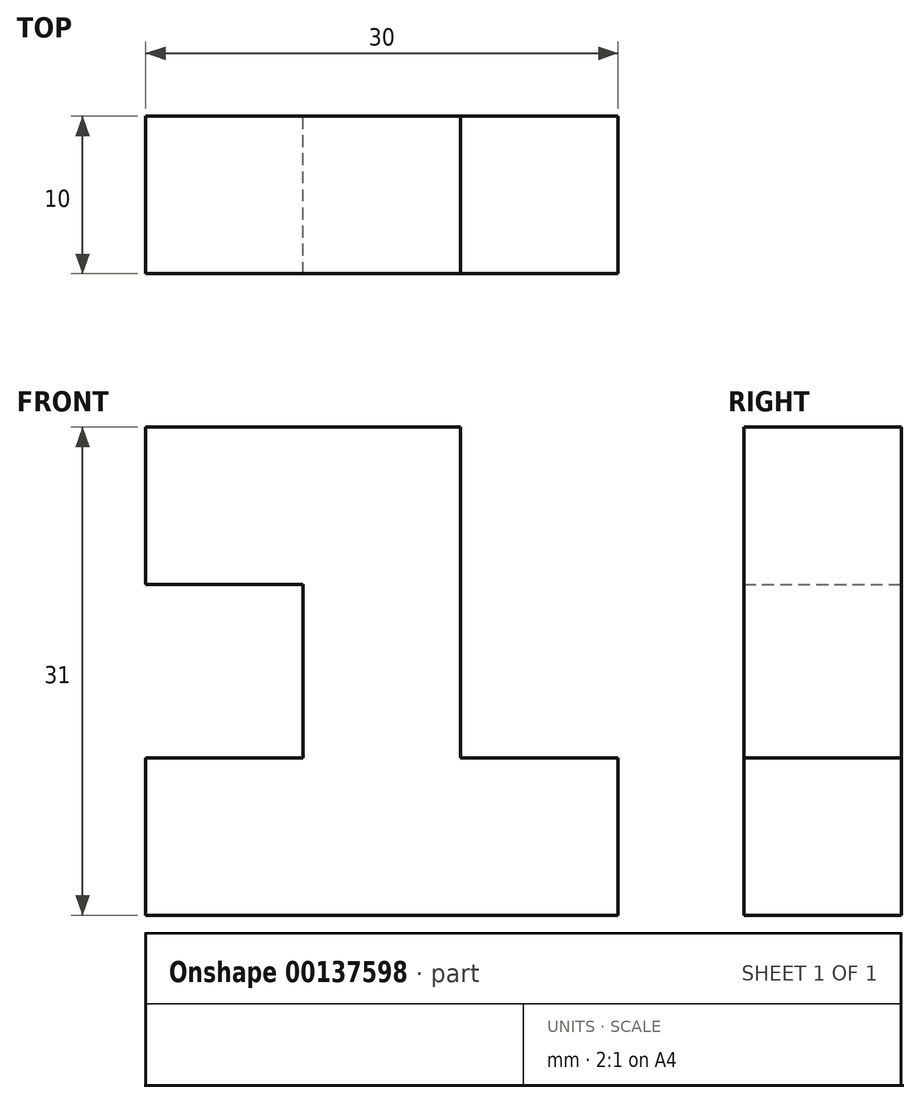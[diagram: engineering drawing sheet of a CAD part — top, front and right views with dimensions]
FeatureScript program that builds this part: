
annotation { "Feature Type Name" : "Feature", "Feature Type Description" : "" }
export const myFeature = defineFeature(function(context is Context, id is Id, definition is map)
    precondition{}
    {
        {
            var Q0;
            Q0=qCreatedBy(makeId("Front.planeOp"),FACE);
            var sketch = newSketch(context, id + "F0", { "sketchPlane" : qUnion([Q0])});
            skLineSegment(sketch, "E0", {"start": v(-31, 40.15) * mm, "end": v(-31, 30.15) * mm});
            skLineSegment(sketch, "E1", {"start": v(-21, 30.15) * mm, "end": v(-31, 30.15) * mm});
            skLineSegment(sketch, "E2", {"start": v(-21, 30.15) * mm, "end": v(-21, 19.15) * mm});
            skLineSegment(sketch, "E3", {"start": v(-21, 19.15) * mm, "end": v(-31, 19.15) * mm});
            skLineSegment(sketch, "E4", {"start": v(-31, 19.15) * mm, "end": v(-31, 9.15) * mm});
            skLineSegment(sketch, "E5", {"start": v(-31, 9.15) * mm, "end": v(-1, 9.15) * mm});
            skLineSegment(sketch, "E6", {"start": v(-1, 9.15) * mm, "end": v(-1, 19.15) * mm});
            skLineSegment(sketch, "E7", {"start": v(-1, 19.15) * mm, "end": v(-11, 19.15) * mm});
            skLineSegment(sketch, "E8", {"start": v(-11, 19.15) * mm, "end": v(-11, 40.15) * mm});
            skLineSegment(sketch, "E9", {"start": v(-11, 40.15) * mm, "end": v(-31, 40.15) * mm});
            skSolve(sketch);
        }
        {
            var Q0;
            Q0=makeQuery(id+"F0.imprint","IMPRINT",FACE,{"disambiguationData":[TD([[makeQuery(id+"F0.imprint","IMPRINT",EDGE,{"derivedFrom":sQuery(id+"F0.wireOp",EDGE,"E0")}),1.0]])]});
            extrude(context, id + "F1", {"entities" : qUnion([Q0]), "depth" : 10 * mm});
        }
    });
